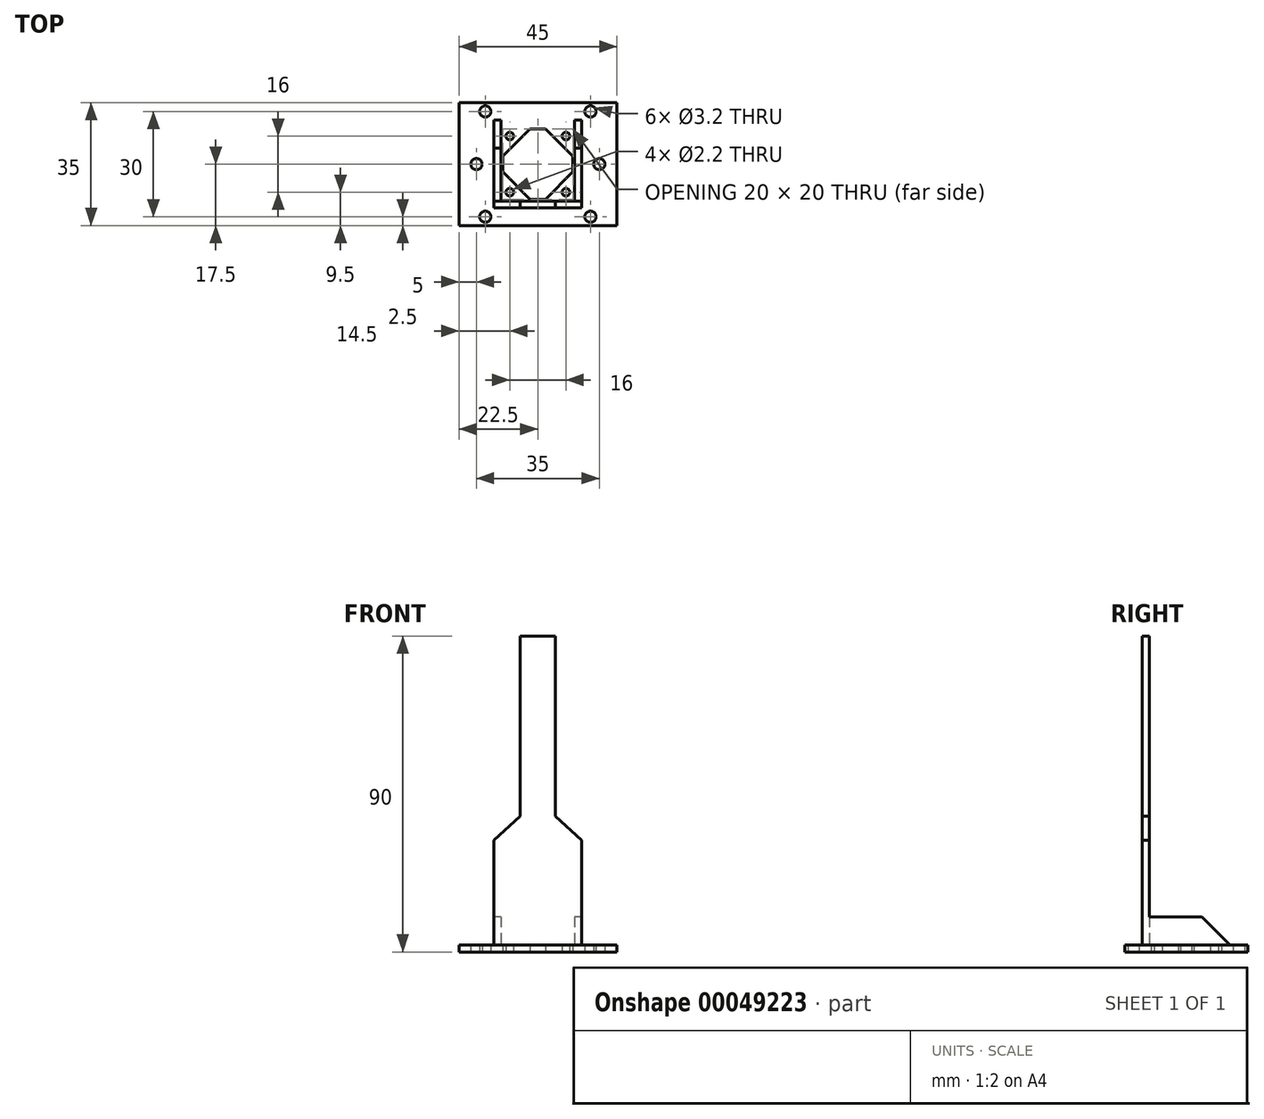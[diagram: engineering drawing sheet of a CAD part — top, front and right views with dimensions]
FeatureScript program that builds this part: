
annotation { "Feature Type Name" : "Feature", "Feature Type Description" : "" }
export const myFeature = defineFeature(function(context is Context, id is Id, definition is map)
    precondition{}
    {
        {
            var Q0;
            Q0=qCreatedBy(makeId("Top.planeOp"),FACE);
            var sketch = newSketch(context, id + "F0", { "sketchPlane" : qUnion([Q0])});
            skLineSegment(sketch, "E0.bottom", {"start": v(10, -10) * mm, "end": v(-10, -10) * mm});
            skLineSegment(sketch, "E0.top", {"start": v(10, 10) * mm, "end": v(-10, 10) * mm});
            skLineSegment(sketch, "E0.left", {"start": v(10, -10) * mm, "end": v(10, 10) * mm});
            skLineSegment(sketch, "E0.right", {"start": v(-10, -10) * mm, "end": v(-10, 10) * mm});
            skPoint(sketch, "E0.middle", {"position": v(0, 0) * mm});
            skCircle(sketch, "E1", {"center": v(-8, 8) * mm, "radius": 1 * mm});
            skCircle(sketch, "E2", {"center": v(8, 8) * mm, "radius": 1 * mm});
            skCircle(sketch, "E3", {"center": v(8, -8) * mm, "radius": 1 * mm});
            skCircle(sketch, "E4", {"center": v(-8, -8) * mm, "radius": 1 * mm});
            skLineSegment(sketch, "E5", {"start": v(-8, 8) * mm, "end": v(8, -8) * mm, "construction": true});
            skLineSegment(sketch, "E6", {"start": v(8, 8) * mm, "end": v(-8, -8) * mm, "construction": true});
            skCircle(sketch, "E7", {"center": v(0, 0) * mm, "radius": 7.5 * mm});
            skSolve(sketch);
        }
        {
            var Q0;
            Q0=qCreatedBy(makeId("Top.planeOp"),FACE);
            var sketch = newSketch(context, id + "F1", { "sketchPlane" : qUnion([Q0])});
            skCircle(sketch, "E8", {"center": v(-8, 8) * mm, "radius": 1.1 * mm});
            skCircle(sketch, "E9", {"center": v(8, 8) * mm, "radius": 1.1 * mm});
            skCircle(sketch, "E10", {"center": v(8, -8) * mm, "radius": 1.1 * mm});
            skCircle(sketch, "E11", {"center": v(-8, -8) * mm, "radius": 1.1 * mm});
            skLineSegment(sketch, "E12", {"start": v(-2.22, 10) * mm, "end": v(-10, 2.22) * mm});
            skLineSegment(sketch, "E13", {"start": v(-10, 2.22) * mm, "end": v(-10, -2.22) * mm});
            skLineSegment(sketch, "E14", {"start": v(-10, -2.22) * mm, "end": v(-2.22, -10) * mm});
            skLineSegment(sketch, "E15", {"start": v(-2.22, -10) * mm, "end": v(2.22, -10) * mm});
            skLineSegment(sketch, "E16", {"start": v(2.22, -10) * mm, "end": v(10, -2.22) * mm});
            skLineSegment(sketch, "E17", {"start": v(10, -2.22) * mm, "end": v(10, 2.22) * mm});
            skLineSegment(sketch, "E18", {"start": v(10, 2.22) * mm, "end": v(2.22, 10) * mm});
            skLineSegment(sketch, "E19", {"start": v(2.22, 10) * mm, "end": v(-2.22, 10) * mm});
            skLineSegment(sketch, "E20.bottom", {"start": v(-12.5, 12.5) * mm, "end": v(12.5, 12.5) * mm});
            skLineSegment(sketch, "E20.top", {"start": v(-12.5, -12.5) * mm, "end": v(12.5, -12.5) * mm});
            skLineSegment(sketch, "E20.left", {"start": v(-12.5, 12.5) * mm, "end": v(-12.5, -12.5) * mm});
            skLineSegment(sketch, "E20.right", {"start": v(12.5, 12.5) * mm, "end": v(12.5, -12.5) * mm});
            skLineSegment(sketch, "E21.bottom", {"start": v(-10.5, 10.5) * mm, "end": v(10.5, 10.5) * mm});
            skLineSegment(sketch, "E21.top", {"start": v(-10.5, -10.5) * mm, "end": v(10.5, -10.5) * mm});
            skLineSegment(sketch, "E21.left", {"start": v(-10.5, 10.5) * mm, "end": v(-10.5, -10.5) * mm});
            skLineSegment(sketch, "E21.right", {"start": v(10.5, 10.5) * mm, "end": v(10.5, -10.5) * mm});
            skLineSegment(sketch, "E22", {"start": v(-10.5, -10.5) * mm, "end": v(-12.5, -10.5) * mm});
            skLineSegment(sketch, "E23", {"start": v(10.5, -10.5) * mm, "end": v(12.5, -10.5) * mm});
            skLineSegment(sketch, "E24", {"start": v(-10.5, 10.5) * mm, "end": v(-10.5, 12.5) * mm});
            skLineSegment(sketch, "E25", {"start": v(10.5, 10.5) * mm, "end": v(10.5, 12.5) * mm});
            skLineSegment(sketch, "E26.bottom", {"start": v(-12.5, 7.85) * mm, "end": v(-22.5, 7.85) * mm});
            skLineSegment(sketch, "E26.top", {"start": v(-12.5, -7.15) * mm, "end": v(-22.5, -7.15) * mm});
            skLineSegment(sketch, "E26.left", {"start": v(-12.5, 7.85) * mm, "end": v(-12.5, -7.15) * mm});
            skLineSegment(sketch, "E26.right", {"start": v(-22.5, 7.85) * mm, "end": v(-22.5, -7.15) * mm});
            skLineSegment(sketch, "E27.bottom", {"start": v(12.5, 7.85) * mm, "end": v(22.5, 7.85) * mm});
            skLineSegment(sketch, "E27.top", {"start": v(12.5, -7.15) * mm, "end": v(22.5, -7.15) * mm});
            skLineSegment(sketch, "E27.left", {"start": v(12.5, 7.85) * mm, "end": v(12.5, -7.15) * mm});
            skLineSegment(sketch, "E27.right", {"start": v(22.5, 7.85) * mm, "end": v(22.5, -7.15) * mm});
            skCircle(sketch, "E28", {"center": v(-17.5, 0) * mm, "radius": 1.6 * mm});
            skPoint(sketch, "E28.centerSnap0", {"position": v(-17.5, 7.85) * mm});
            skCircle(sketch, "E29", {"center": v(17.5, 0) * mm, "radius": 1.6 * mm});
            skLineSegment(sketch, "E30.bottom", {"start": v(-22.5, -17.5) * mm, "end": v(22.5, -17.5) * mm});
            skLineSegment(sketch, "E30.top", {"start": v(-22.5, 17.5) * mm, "end": v(22.5, 17.5) * mm});
            skLineSegment(sketch, "E30.left", {"start": v(-22.5, -17.5) * mm, "end": v(-22.5, 17.5) * mm});
            skLineSegment(sketch, "E30.right", {"start": v(22.5, -17.5) * mm, "end": v(22.5, 17.5) * mm});
            skCircle(sketch, "E31", {"center": v(-15, 15) * mm, "radius": 1.6 * mm});
            skCircle(sketch, "E32", {"center": v(15, 15) * mm, "radius": 1.6 * mm});
            skCircle(sketch, "E33", {"center": v(15, -15) * mm, "radius": 1.6 * mm});
            skCircle(sketch, "E34", {"center": v(-15, -15) * mm, "radius": 1.6 * mm});
            skLineSegment(sketch, "E35", {"start": v(15, -15) * mm, "end": v(-15, 15) * mm, "construction": true});
            skLineSegment(sketch, "E36", {"start": v(-15, -15) * mm, "end": v(15, 15) * mm, "construction": true});
            skLineSegment(sketch, "E37", {"start": v(0, 0) * mm, "end": v(0, 17.5) * mm, "construction": true});
            skLineSegment(sketch, "E38", {"start": v(0, 0) * mm, "end": v(0, -17.5) * mm, "construction": true});
            skSolve(sketch);
        }
        {
            var Q0;
            Q0=makeQuery(id+"F1.imprint","IMPRINT",FACE,{"disambiguationData":[TD([[makeQuery(id+"F1.imprint","IMPRINT",EDGE,{"derivedFrom":sQuery(id+"F1.wireOp",EDGE,"E8")}),-1.0]])]});
            var Q1;
            Q1=makeQuery(id+"F1.imprint","IMPRINT",FACE,{"disambiguationData":[TD([[makeQuery(id+"F1.imprint","IMPRINT",EDGE,{"derivedFrom":sQuery(id+"F1.wireOp",EDGE,"E20.bottom")}),-1.0]])]});
            var Q2;
            Q2=makeQuery(id+"F1.imprint","IMPRINT",FACE,{"disambiguationData":[TD([[makeQuery(id+"F1.imprint","IMPRINT",EDGE,{"derivedFrom":sQuery(id+"F1.wireOp",EDGE,"E21.left")}),-1.0]])]});
            var Q3;
            Q3=makeQuery(id+"F1.imprint","IMPRINT",FACE,{"disambiguationData":[TD([[makeQuery(id+"F1.imprint","IMPRINT",EDGE,{"derivedFrom":sQuery(id+"F1.wireOp",EDGE,"E21.right")}),1.0]])]});
            var Q4;
            Q4=makeQuery(id+"F1.imprint","IMPRINT",FACE,{"disambiguationData":[TD([[makeQuery(id+"F1.imprint","IMPRINT",EDGE,{"derivedFrom":sQuery(id+"F1.wireOp",EDGE,"E26.bottom")}),1.0]])]});
            var Q5;
            Q5=makeQuery(id+"F1.imprint","IMPRINT",FACE,{"disambiguationData":[TD([[makeQuery(id+"F1.imprint","IMPRINT",EDGE,{"derivedFrom":sQuery(id+"F1.wireOp",EDGE,"E27.bottom")}),-1.0]])]});
            var Q6;
            {var subQ1=sQuery(id+"F1.wireOp",EDGE,"E26.bottom");Q6=makeQuery(id+"F1.imprint","IMPRINT",FACE,{"disambiguationData":[TD([[makeQuery(id+"F1.imprint","IMPRINT",EDGE,{"derivedFrom":subQ1}),-1.0]])]});}
            var Q7;
            {var subQ1=sQuery(id+"F1.wireOp",EDGE,"E20.top");Q7=makeQuery(id+"F1.imprint","IMPRINT",FACE,{"disambiguationData":[TD([[makeQuery(id+"F1.imprint","IMPRINT",EDGE,{"derivedFrom":subQ1}),-1.0]])]});}
            var Q8;
            {var subQ1=sQuery(id+"F1.wireOp",EDGE,"E20.top");Q8=makeQuery(id+"F1.imprint","IMPRINT",FACE,{"disambiguationData":[TD([[makeQuery(id+"F1.imprint","IMPRINT",EDGE,{"derivedFrom":subQ1}),1.0]])]});}
            extrude(context, id + "F2", {"entities" : qUnion([Q0, Q1, Q2, Q3, Q4, Q5, Q6, Q7, Q8]), "depth" : 2 * mm, "offsetDistance" : 25 * mm});
        }
        {
            var Q0;
            {var subQ1=sQuery(id+"F1.wireOp",EDGE,"E20.top");Q0=makeQuery(id+"F1.imprint","IMPRINT",FACE,{"disambiguationData":[TD([[makeQuery(id+"F1.imprint","IMPRINT",EDGE,{"derivedFrom":subQ1}),1.0]])]});}
            extrude(context, id + "F3", {"entities" : qUnion([Q0]), "operationType" : NewBodyOperationType.ADD, "depth" : 90 * mm, "offsetDistance" : 25 * mm});
        }
        {
            var Q0;
            Q0=makeQuery(id+"F1.imprint","IMPRINT",FACE,{"disambiguationData":[TD([[makeQuery(id+"F1.imprint","IMPRINT",EDGE,{"derivedFrom":sQuery(id+"F1.wireOp",EDGE,"E21.right")}),1.0]])]});
            var Q1;
            Q1=makeQuery(id+"F1.imprint","IMPRINT",FACE,{"disambiguationData":[TD([[makeQuery(id+"F1.imprint","IMPRINT",EDGE,{"derivedFrom":sQuery(id+"F1.wireOp",EDGE,"E21.left")}),-1.0]])]});
            var Q2;
            {var subQ1=sQuery(id+"F1.wireOp",EDGE,"E20.top");Q2=makeQuery(id+"F1.imprint","IMPRINT",FACE,{"disambiguationData":[TD([[makeQuery(id+"F1.imprint","IMPRINT",EDGE,{"derivedFrom":subQ1}),1.0]])]});}
            extrude(context, id + "F4", {"entities" : qUnion([Q0, Q1, Q2]), "operationType" : NewBodyOperationType.ADD, "depth" : 10 * mm, "offsetDistance" : 25 * mm});
        }
        {
            var Q0;
            {var subQ0=sQuery(id+"F1.wireOp",EDGE,"E20.bottom");Q0=makeQuery(id+"F4.opExtrude","CAP_EDGE",EDGE,{"disambiguationData":[OSD([subQ0]),TDD([makeQuery(id+"F1.imprint","IMPRINT",EDGE,{"disambiguationData":[TD([[makeQuery(id+"F1.imprint","INTERSECT",VERTEX,{"derivedFrom":[subQ0,sQuery(id+"F1.wireOp",EDGE,"E20.right")]}),1.0]])],"derivedFrom":subQ0})])],"isStart":false});}
            var Q1;
            {var subQ0=sQuery(id+"F1.wireOp",EDGE,"E20.bottom");Q1=makeQuery(id+"F4.opExtrude","CAP_EDGE",EDGE,{"disambiguationData":[OSD([subQ0]),TDD([makeQuery(id+"F1.imprint","IMPRINT",EDGE,{"disambiguationData":[TD([[makeQuery(id+"F1.imprint","INTERSECT",VERTEX,{"derivedFrom":[subQ0,sQuery(id+"F1.wireOp",EDGE,"E20.left")]}),-1.0]])],"derivedFrom":subQ0})])],"isStart":false});}
            chamfer(context, id + "F5", {"entities" : qUnion([Q0, Q1]), "width" : 8 * mm, "tangentPropagation" : true});
        }
        {
            var Q0;
            Q0=makeQuery(id+"F3.opExtrude","SWEPT_FACE",FACE,{"disambiguationData":[OSD([sQuery(id+"F1.wireOp",EDGE,"E21.top"),sQuery(id+"F1.wireOp",EDGE,"E22"),sQuery(id+"F1.wireOp",EDGE,"E23")])]});
            var sketch = newSketch(context, id + "F6", { "sketchPlane" : qUnion([Q0])});
            skLineSegment(sketch, "E39", {"start": v(-12.5, 31.77) * mm, "end": v(-5, 38.75) * mm});
            skLineSegment(sketch, "E40", {"start": v(-5, 38.75) * mm, "end": v(-5, 90) * mm});
            skLineSegment(sketch, "E41", {"start": v(-5, 90) * mm, "end": v(-12.5, 90) * mm});
            skLineSegment(sketch, "E42", {"start": v(-12.5, 90) * mm, "end": v(-12.5, 31.77) * mm});
            skLineSegment(sketch, "E43", {"start": v(12.5, 31.77) * mm, "end": v(5, 38.75) * mm});
            skLineSegment(sketch, "E44", {"start": v(5, 38.75) * mm, "end": v(5, 90) * mm});
            skLineSegment(sketch, "E45", {"start": v(5, 90) * mm, "end": v(12.5, 90) * mm});
            skLineSegment(sketch, "E46", {"start": v(12.5, 90) * mm, "end": v(12.5, 31.77) * mm});
            skSolve(sketch);
        }
        {
            var Q0;
            Q0 = qSketchRegion(id + "F6", true);
            extrude(context, id + "F7", {"entities" : qUnion([Q0]), "operationType" : NewBodyOperationType.REMOVE, "oppositeDirection" : true, "depth" : 25 * mm, "offsetDistance" : 25 * mm});
        }
    });
